# Revit family: Speckle_Water_Tank
name_source: partatom
category: Plumbing Fixtures
units: mm (PartAtom-declared; Revit-internal decimal feet)

## family parameters
Always vertical = Yes
Cut with Voids When Loaded = No
Part Type = Normal
Room Calculation Point = No
Round Connector Dimension = Use Diameter
Shared = No
Work Plane-Based = No

## types (1)
- TVC-2700 lt
    D = 1550 mm  [stored 5.0853 ft]
    D INT B = 1545 mm
    D INT TAPA = 550 mm
    Default Elevation = 0 mm  [stored 0 ft]
    Desarrollador = http://www.rzm.mx
    Description = Agua
    H CUADRO = 75 mm
    H CUERPO = 1200 mm
    H CUERPO TAPA = 100 mm  [stored 0.328084 ft]
    Keynote = 25.03
    L = 1600 mm  [stored 5.24934 ft]
    R = 775 mm  [stored 2.54265 ft]
    R CURV TAPA = 6 mm  [stored 0.019685 ft]
    R ESQUINA = 25 mm  [stored 0.082021 ft]
    R S ESP = 8 mm  [stored 0.0262467 ft]
    R SALIDA = 6 mm  [stored 0.019685 ft]
    SAP = 550137
    Type Comments = Tanque de PVC 2700ltrs
    Type Image = <None>
    URL = http://www.rotoplas.com.mx

note: [stored X ft] marks values corroborated as IEEE doubles in the binary element streams (Revit-internal decimal feet)

## geometry (parser evidence)
native form markers: Sweep x2
no freeform markers — native parametric forms only
